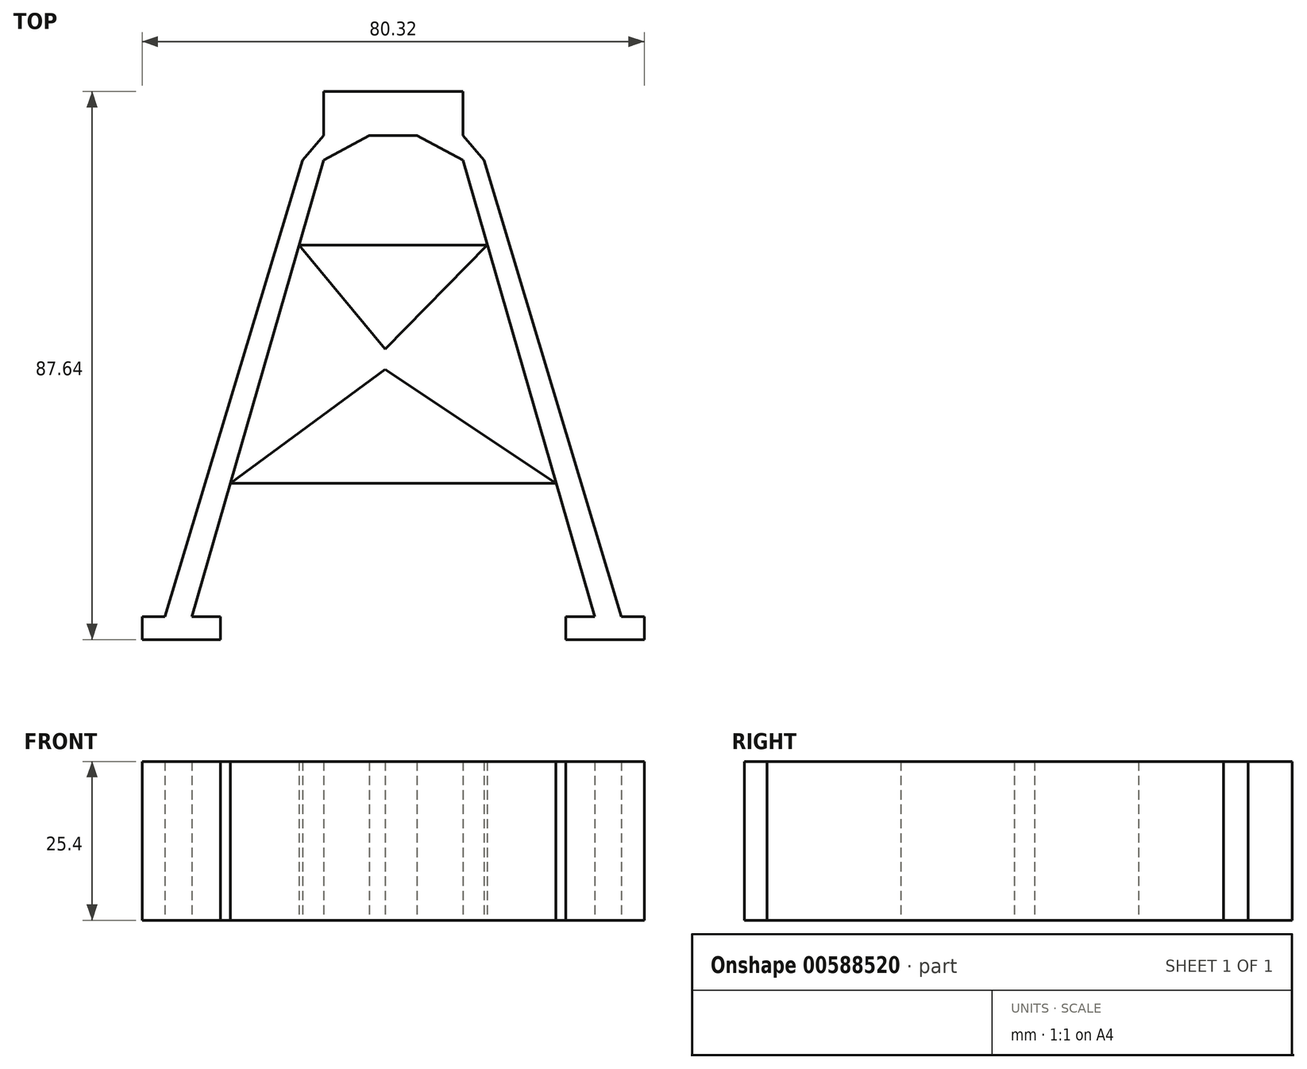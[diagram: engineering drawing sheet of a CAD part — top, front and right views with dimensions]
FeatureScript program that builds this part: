
annotation { "Feature Type Name" : "Feature", "Feature Type Description" : "" }
export const myFeature = defineFeature(function(context is Context, id is Id, definition is map)
    precondition{}
    {
        {
            var Q0;
            Q0=qCreatedBy(makeId("Top.planeOp"),FACE);
            var sketch = newSketch(context, id + "F0", { "sketchPlane" : qUnion([Q0])});
            skLineSegment(sketch, "E0", {"start": v(-14.5, 43.52) * mm, "end": v(-36.5, -29.47) * mm});
            skLineSegment(sketch, "E1", {"start": v(-36.5, -29.47) * mm, "end": v(-40.16, -29.47) * mm});
            skLineSegment(sketch, "E2", {"start": v(-40.16, -29.47) * mm, "end": v(-40.16, -33.13) * mm});
            skLineSegment(sketch, "E3", {"start": v(-40.16, -33.13) * mm, "end": v(-27.64, -33.13) * mm});
            skLineSegment(sketch, "E4", {"start": v(-27.64, -33.13) * mm, "end": v(-27.64, -29.47) * mm});
            skLineSegment(sketch, "E5", {"start": v(-27.64, -29.47) * mm, "end": v(-32.22, -29.47) * mm});
            skLineSegment(sketch, "E6", {"start": v(-32.22, -29.47) * mm, "end": v(-11.15, 43.52) * mm});
            skLineSegment(sketch, "E7", {"start": v(-14.5, 43.52) * mm, "end": v(-11.15, 47.49) * mm});
            skLineSegment(sketch, "E8", {"start": v(-11.15, 54.51) * mm, "end": v(-11.15, 47.49) * mm});
            skLineSegment(sketch, "E9", {"start": v(-11.15, 43.52) * mm, "end": v(-3.82, 47.49) * mm});
            skLineSegment(sketch, "E10", {"start": v(-11.15, 54.51) * mm, "end": v(0, 54.51) * mm});
            skLineSegment(sketch, "E11", {"start": v(-3.82, 47.49) * mm, "end": v(0, 47.49) * mm});
            skLineSegment(sketch, "E12", {"start": v(0, 54.51) * mm, "end": v(0, -34.36) * mm});
            skPoint(sketch, "E13.end.orphan", {"position": v(13, 43.52) * mm});
            skPoint(sketch, "E14.start.orphan", {"position": v(10.84, 47.49) * mm});
            skLineSegment(sketch, "E15.MirrorCS", {"start": v(11.15, 43.52) * mm, "end": v(3.82, 47.49) * mm});
            skLineSegment(sketch, "E16.MirrorCS", {"start": v(11.15, 54.51) * mm, "end": v(11.15, 47.49) * mm});
            skLineSegment(sketch, "E17.MirrorCS", {"start": v(11.15, 54.51) * mm, "end": v(0, 54.51) * mm});
            skLineSegment(sketch, "E18.MirrorCS", {"start": v(14.5, 43.52) * mm, "end": v(36.5, -29.47) * mm});
            skLineSegment(sketch, "E19.MirrorCS", {"start": v(32.22, -29.47) * mm, "end": v(11.15, 43.52) * mm});
            skLineSegment(sketch, "E20.MirrorCS", {"start": v(40.16, -33.13) * mm, "end": v(27.64, -33.13) * mm});
            skLineSegment(sketch, "E21", {"start": v(11.15, 47.49) * mm, "end": v(14.5, 43.52) * mm});
            skLineSegment(sketch, "E22", {"start": v(36.5, -29.47) * mm, "end": v(40.16, -29.47) * mm});
            skLineSegment(sketch, "E23", {"start": v(40.16, -29.47) * mm, "end": v(40.16, -33.13) * mm});
            skLineSegment(sketch, "E24", {"start": v(27.64, -33.13) * mm, "end": v(27.64, -29.47) * mm});
            skLineSegment(sketch, "E25", {"start": v(27.64, -29.47) * mm, "end": v(32.22, -29.47) * mm});
            skLineSegment(sketch, "E26", {"start": v(3.82, 47.49) * mm, "end": v(0, 47.49) * mm});
            skLineSegment(sketch, "E27", {"start": v(-7.48, 54.51) * mm, "end": v(-1.3, 65.93) * mm});
            skPoint(sketch, "E27.startSnap0", {"position": v(-7.48, 45.5) * mm});
            skLineSegment(sketch, "E28", {"start": v(8.4, 54.51) * mm, "end": v(2.6, 65.93) * mm});
            skLineSegment(sketch, "E29", {"start": v(2.6, 65.93) * mm, "end": v(-1.3, 65.93) * mm});
            skLineSegment(sketch, "E30", {"start": v(-1.3, 65.93) * mm, "end": v(-5.04, 65.93) * mm});
            skLineSegment(sketch, "E31", {"start": v(-5.04, 65.93) * mm, "end": v(-5.04, 69.78) * mm});
            skLineSegment(sketch, "E32", {"start": v(-5.04, 69.78) * mm, "end": v(-1.3, 69.78) * mm});
            skLineSegment(sketch, "E33", {"start": v(-1.3, 69.78) * mm, "end": v(5.04, 69.78) * mm});
            skLineSegment(sketch, "E34", {"start": v(5.04, 69.78) * mm, "end": v(5.04, 65.93) * mm});
            skLineSegment(sketch, "E35", {"start": v(5.04, 65.93) * mm, "end": v(2.6, 65.93) * mm});
            skLineSegment(sketch, "E36", {"start": v(15.07, 29.94) * mm, "end": v(-15.07, 29.94) * mm});
            skLineSegment(sketch, "E37", {"start": v(-15.07, 29.94) * mm, "end": v(-26.05, -8.1) * mm});
            skLineSegment(sketch, "E38", {"start": v(-26.05, -8.1) * mm, "end": v(26.05, -8.1) * mm});
            skLineSegment(sketch, "E39", {"start": v(26.05, -8.1) * mm, "end": v(19.86, 13.33) * mm});
            skLineSegment(sketch, "E40", {"start": v(19.86, 13.33) * mm, "end": v(-19.86, 13.33) * mm});
            skLineSegment(sketch, "E41", {"start": v(-15.07, 29.94) * mm, "end": v(-1.3, 13.33) * mm});
            skLineSegment(sketch, "E42", {"start": v(-1.3, 13.33) * mm, "end": v(15.07, 29.94) * mm});
            skLineSegment(sketch, "E43", {"start": v(26.05, -8.1) * mm, "end": v(-1.3, 10.08) * mm});
            skPoint(sketch, "E43.endSnap0", {"position": v(0, 10.08) * mm});
            skLineSegment(sketch, "E44", {"start": v(-1.3, 10.08) * mm, "end": v(-26.05, -8.1) * mm});
            skSolve(sketch);
        }
        {
            var Q0;
            Q0=makeQuery(id+"F0.imprint","IMPRINT",FACE,{"disambiguationData":[TD([[makeQuery(id+"F0.imprint","IMPRINT",EDGE,{"derivedFrom":sQuery(id+"F0.wireOp",EDGE,"E0")}),1.0]])]});
            var Q1;
            {var subQ9=sQuery(id+"F0.wireOp",EDGE,"E16.MirrorCS");Q1=makeQuery(id+"F0.imprint","IMPRINT",FACE,{"disambiguationData":[TD([[makeQuery(id+"F0.imprint","IMPRINT",EDGE,{"derivedFrom":subQ9}),-1.0]])]});}
            var Q2;
            {var subQ0=sQuery(id+"F0.wireOp",EDGE,"E36");var subQ1=sQuery(id+"F0.wireOp",EDGE,"E12");var subQ2=makeQuery(id+"F0.imprint","INTERSECT",VERTEX,{"derivedFrom":[subQ1,subQ0]});Q2=makeQuery(id+"F0.imprint","IMPRINT",FACE,{"disambiguationData":[TD([[makeQuery(id+"F0.imprint","IMPRINT",EDGE,{"disambiguationData":[TD([[subQ2,-1.0]])],"derivedFrom":subQ1}),1.0]])]});}
            var Q3;
            {var subQ5=sQuery(id+"F0.wireOp",EDGE,"E41");Q3=makeQuery(id+"F0.imprint","IMPRINT",FACE,{"disambiguationData":[TD([[makeQuery(id+"F0.imprint","IMPRINT",EDGE,{"derivedFrom":subQ5}),1.0]])]});}
            var Q4;
            {var subQ0=sQuery(id+"F0.wireOp",EDGE,"E38");var subQ1=sQuery(id+"F0.wireOp",EDGE,"E12");var subQ2=makeQuery(id+"F0.imprint","INTERSECT",VERTEX,{"derivedFrom":[subQ1,subQ0]});Q4=makeQuery(id+"F0.imprint","IMPRINT",FACE,{"disambiguationData":[TD([[makeQuery(id+"F0.imprint","IMPRINT",EDGE,{"disambiguationData":[TD([[subQ2,1.0]])],"derivedFrom":subQ1}),1.0]])]});}
            var Q5;
            {var subQ5=sQuery(id+"F0.wireOp",EDGE,"E44");Q5=makeQuery(id+"F0.imprint","IMPRINT",FACE,{"disambiguationData":[TD([[makeQuery(id+"F0.imprint","IMPRINT",EDGE,{"derivedFrom":subQ5}),1.0]])]});}
            extrude(context, id + "F1", {"entities" : qUnion([Q0, Q1, Q2, Q3, Q4, Q5]), "depth" : 25.4 * mm, "offsetDistance" : 25.4 * mm});
        }
    });
